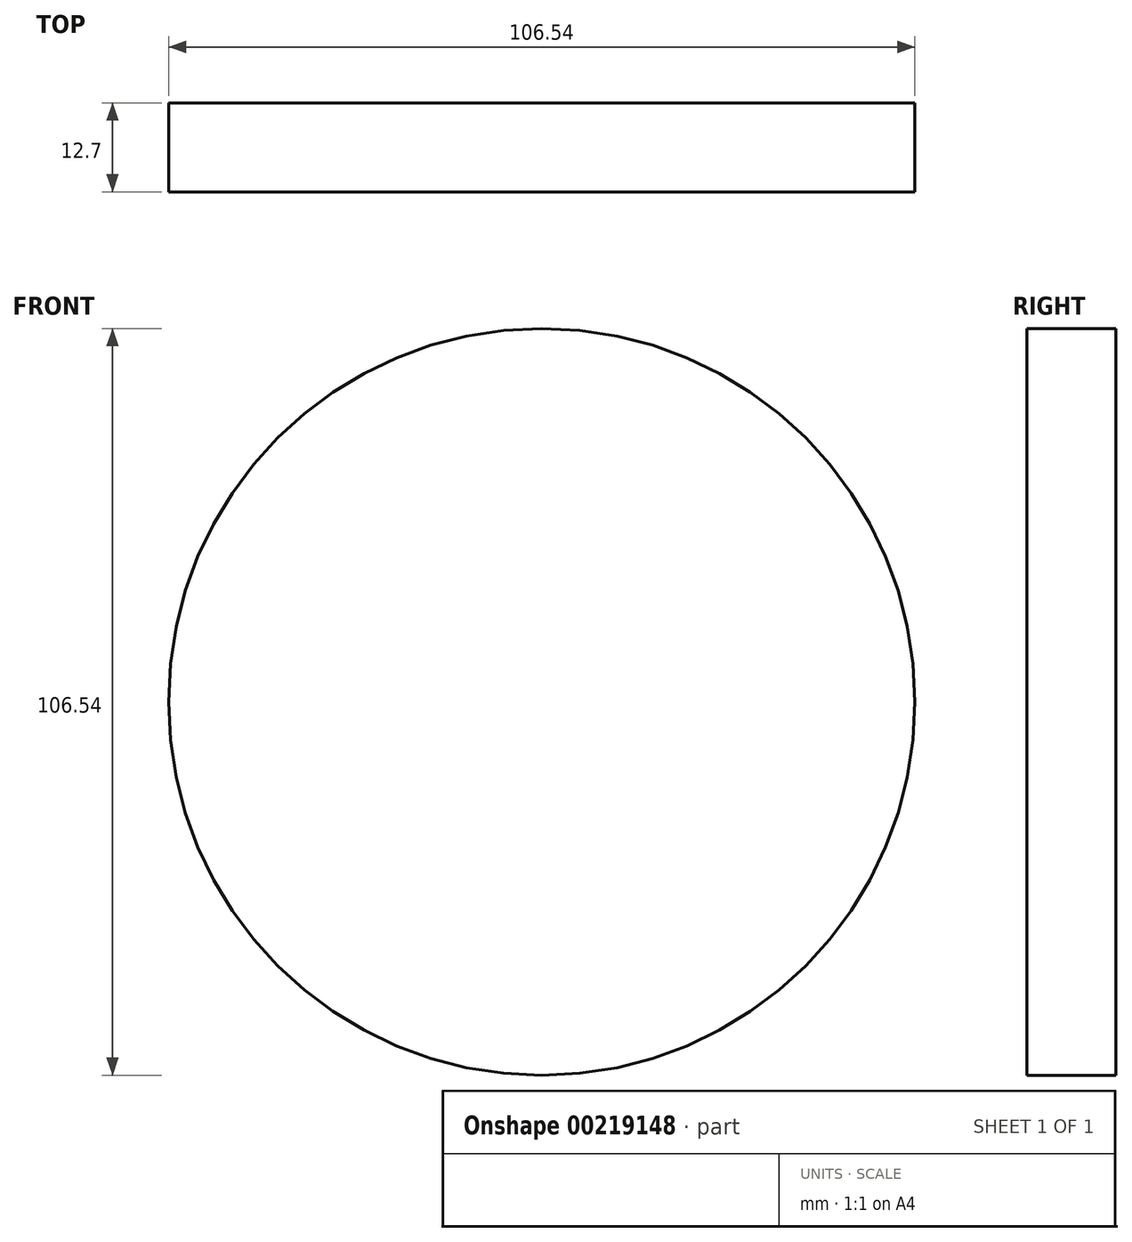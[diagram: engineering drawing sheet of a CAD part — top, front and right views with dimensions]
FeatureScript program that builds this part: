
annotation { "Feature Type Name" : "Feature", "Feature Type Description" : "" }
export const myFeature = defineFeature(function(context is Context, id is Id, definition is map)
    precondition{}
    {
        {
            var Q0;
            Q0=qCreatedBy(makeId("Front.planeOp"),FACE);
            var sketch = newSketch(context, id + "F0", { "sketchPlane" : qUnion([Q0])});
            skCircle(sketch, "E0", {"center": v(0, 0) * mm, "radius": 53.27 * mm});
            skCircle(sketch, "E1", {"center": v(0, 0) * mm, "radius": 35.32 * mm});
            skSolve(sketch);
        }
        {
            var Q0;
            Q0=makeQuery(id+"F0.imprint","IMPRINT",FACE,{"disambiguationData":[TD([[makeQuery(id+"F0.imprint","IMPRINT",EDGE,{"derivedFrom":sQuery(id+"F0.wireOp",EDGE,"E0")}),1.0]])]});
            var Q1;
            Q1=makeQuery(id+"F0.imprint","IMPRINT",FACE,{"disambiguationData":[TD([[makeQuery(id+"F0.imprint","IMPRINT",EDGE,{"derivedFrom":sQuery(id+"F0.wireOp",EDGE,"E1")}),1.0]])]});
            extrude(context, id + "F1", {"entities" : qUnion([Q0, Q1]), "endBound" : BoundingType.SYMMETRIC, "depth" : 12.7 * mm});
        }
    });
